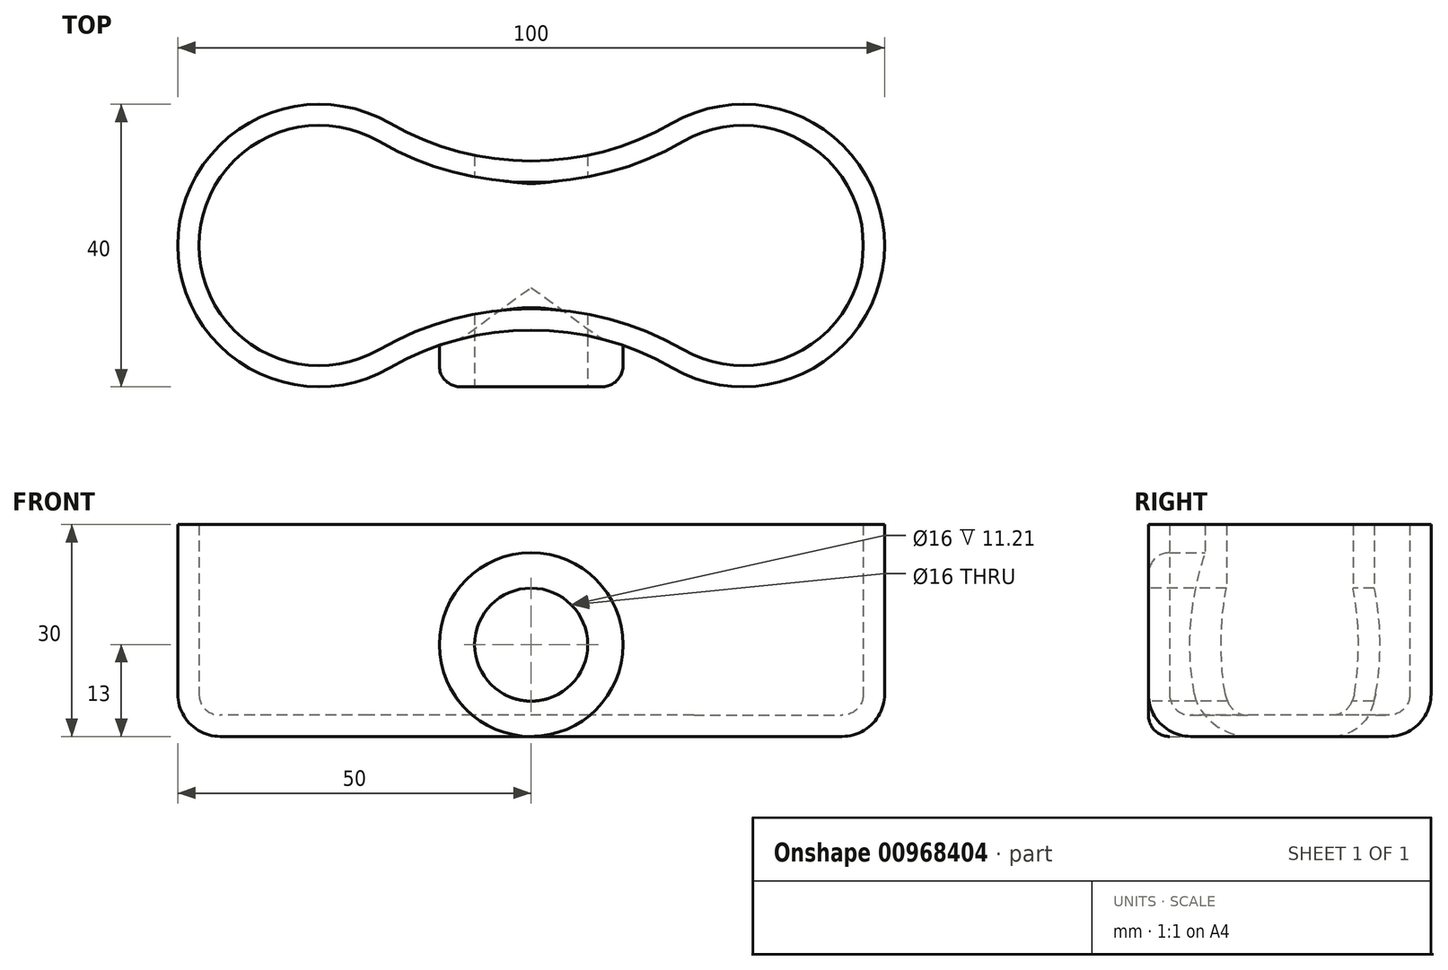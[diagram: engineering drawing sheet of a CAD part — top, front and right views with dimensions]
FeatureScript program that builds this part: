
annotation { "Feature Type Name" : "Feature", "Feature Type Description" : "" }
export const myFeature = defineFeature(function(context is Context, id is Id, definition is map)
    precondition{}
    {
        {
            var Q0;
            Q0=qCreatedBy(makeId("Top.planeOp"),FACE);
            var sketch = newSketch(context, id + "F0", { "sketchPlane" : qUnion([Q0])});
            skArc(sketch, "E0", {"start": v(-20, 17.32) * mm, "mid": v(-50, 0) * mm, "end": v(-20, -17.32) * mm});
            skArc(sketch, "E1", {"start": v(20, -17.32) * mm, "mid": v(50, 0) * mm, "end": v(20, 17.32) * mm});
            skArc(sketch, "E2", {"start": v(-20, 17.32) * mm, "mid": v(0, 11.96) * mm, "end": v(20, 17.32) * mm});
            skArc(sketch, "E3.MirrorCS", {"start": v(-20, -17.32) * mm, "mid": v(0, -11.96) * mm, "end": v(20, -17.32) * mm});
            skCircle(sketch, "E4", {"center": v(-30, 0) * mm, "radius": 11 * mm});
            skCircle(sketch, "E5", {"center": v(30, 0) * mm, "radius": 11 * mm});
            skSolve(sketch);
        }
        {
            var Q0;
            Q0=qCreatedBy(makeId("Front.planeOp"),FACE);
            var sketch = newSketch(context, id + "F1", { "sketchPlane" : qUnion([Q0])});
            skCircle(sketch, "E6", {"center": v(0, 13) * mm, "radius": 13 * mm});
            skCircle(sketch, "E7", {"center": v(0, 13) * mm, "radius": 8 * mm});
            skSolve(sketch);
        }
        {
            var Q0;
            Q0 = qSketchRegion(id + "F0", true);
            var Q1;
            Q1=makeQuery(id+"F0.imprint","IMPRINT",FACE,{"disambiguationData":[TD([[makeQuery(id+"F0.imprint","IMPRINT",EDGE,{"derivedFrom":sQuery(id+"F0.wireOp",EDGE,"3a716cbb-a77d-42e6-bb11-9e72d74131ed.0")}),1.0]])]});
            var Q2;
            Q2=makeQuery(id+"F0.imprint","IMPRINT",FACE,{"disambiguationData":[TD([[makeQuery(id+"F0.imprint","IMPRINT",EDGE,{"derivedFrom":sQuery(id+"F0.wireOp",EDGE,"E4")}),1.0]])]});
            var Q3;
            Q3=makeQuery(id+"F0.imprint","IMPRINT",FACE,{"disambiguationData":[TD([[makeQuery(id+"F0.imprint","IMPRINT",EDGE,{"derivedFrom":sQuery(id+"F0.wireOp",EDGE,"E5")}),1.0]])]});
            extrude(context, id + "F2", {"entities" : qUnion([Q0, Q1, Q2, Q3]), "depth" : 30 * mm, "offsetDistance" : 25 * mm});
        }
        {
            var Q0;
            Q0=makeQuery(id+"F2.opExtrude","CAP_EDGE",EDGE,{"disambiguationData":[OSD([sQuery(id+"F0.wireOp",EDGE,"E0")])],"isStart":true});
            fillet(context, id + "F3", {"entities" : qUnion([Q0]), "tangentPropagation" : true, "radius" : 6 * mm, "defaultsChanged" : true, "vertexSettings" : [], "allowEdgeOverflow" : false});
        }
        {
            var Q0;
            Q0=makeQuery(id+"F2.opExtrude","CAP_FACE",FACE,{"disambiguationData":[OSD([sQuery(id+"F0.wireOp",EDGE,"E0"),sQuery(id+"F0.wireOp",EDGE,"E1"),sQuery(id+"F0.wireOp",EDGE,"E2"),sQuery(id+"F0.wireOp",EDGE,"E3.MirrorCS")])],"isStart":false});
            shell(context, id + "F4", {"entities" : qUnion([Q0]), "thickness" : 3 * mm});
        }
        {
            var Q0;
            Q0=makeQuery(id+"F1.imprint","IMPRINT",FACE,{"disambiguationData":[TD([[makeQuery(id+"F1.imprint","IMPRINT",EDGE,{"derivedFrom":sQuery(id+"F1.wireOp",EDGE,"E6")}),1.0]])]});
            var Q1;
            Q1=makeQuery(id+"F1.imprint","IMPRINT",FACE,{"disambiguationData":[TD([[makeQuery(id+"F1.imprint","IMPRINT",EDGE,{"derivedFrom":sQuery(id+"F1.wireOp",EDGE,"E7")}),1.0]])]});
            var Q2;
            Q2=makeQuery(id+"F2.opExtrude","SWEPT_BODY",BODY,{"disambiguationData":[OSD([sQuery(id+"F0.wireOp",EDGE,"E0"),sQuery(id+"F0.wireOp",EDGE,"E1"),sQuery(id+"F0.wireOp",EDGE,"E2"),sQuery(id+"F0.wireOp",EDGE,"E3.MirrorCS")])]});
            extrude(context, id + "F5", {"entities" : qUnion([Q0, Q1]), "operationType" : NewBodyOperationType.ADD, "depth" : 20 * mm, "offsetDistance" : 25 * mm, "hasSecondDirection" : true, "secondDirectionBound" : BoundingType.UP_TO_BODY, "secondDirectionOppositeDirection" : false, "secondDirectionDepth" : 25 * mm, "secondDirectionBoundEntityBody" : qUnion([Q2])});
        }
        {
            var Q0;
            Q0=makeQuery(id+"FTiIpO5lwhBUe12_1.1.F5.opExtrude","CAP_EDGE",EDGE,{"disambiguationData":[OSD([sQuery(id+"F1.wireOp",EDGE,"E6")]),topologyDisambiguationEdgeConnected([makeQuery(id+"F2.opExtrude","SWEPT_FACE",FACE,{"disambiguationData":[OSD([sQuery(id+"F0.wireOp",EDGE,"E2")])]})])],"isStart":false});
            var Q1;
            Q1=makeQuery(id+"F5.opExtrude","CAP_EDGE",EDGE,{"disambiguationData":[OSD([sQuery(id+"F1.wireOp",EDGE,"E6")]),topologyDisambiguationEdgeConnected([makeQuery(id+"F2.opExtrude","SWEPT_FACE",FACE,{"disambiguationData":[OSD([sQuery(id+"F0.wireOp",EDGE,"E3.MirrorCS")])]})])],"isStart":false});
            fillet(context, id + "F6", {"entities" : qUnion([Q0, Q1]), "tangentPropagation" : true, "radius" : 3 * mm, "defaultsChanged" : false, "vertexSettings" : [], "allowEdgeOverflow" : false});
        }
        {
            var Q0;
            Q0=makeQuery(id+"F1.imprint","IMPRINT",FACE,{"disambiguationData":[TD([[makeQuery(id+"F1.imprint","IMPRINT",EDGE,{"derivedFrom":sQuery(id+"F1.wireOp",EDGE,"E7")}),1.0]])]});
            extrude(context, id + "F7", {"entities" : qUnion([Q0]), "operationType" : NewBodyOperationType.REMOVE, "oppositeDirection" : true, "depth" : 60 * mm, "offsetDistance" : 25 * mm, "symmetric" : true});
        }
    });
